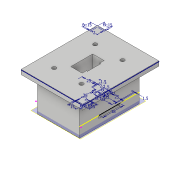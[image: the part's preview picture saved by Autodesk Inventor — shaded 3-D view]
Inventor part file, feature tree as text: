
AUTODESK INVENTOR PART (.ipt)
format: ipt  version: 2017 (Build 210142000, 142)  size: 485,376 bytes
history: native  units: in
note: dims shown in document units (in); Inventor stores cm internally (conversion verified against a paired STEP export)
features: extrude x22, sketch x20, plane x5, fillet x2, other x1, hole x1, chamfer x1
ambient origin geometry x8: Origin, YZ Plane, XZ Plane, XY Plane, X Axis, Y Axis, Z Axis, Center Point
bodies: Solid1 (feature_tree)
feature tree (52):
  plane  "Work Plane1"
  sketch  "Sketch1"  dims[d0=0.9843in d1=0.0067in]
  extrude  "Extrusion1"  Depth=0.0067in
  extrude  "End"  Depth=0.1969in
  extrude  "EndII"  Depth=0.112in
  extrude  "Extrusion4"  Depth=0.112in
  sketch  "Sketch8"  dims[d11=0.1969in d13=0.1969in]
  extrude  "Extrusion8"  Depth=0.1969in
  plane  "Work Plane2"
  sketch  "Sketch12"  dims[d18=2.3278in d19=0.0in d20=0.9843in d21=0.0in]
  other  "Work Point1"
  extrude  "Extrusion10"  Depth=0.9843in TaperAngle=0.0deg
  plane  "Work Plane3"
  extrude  "Extrusion11"  Depth=0.1969in
  plane  "Work Plane4"
  sketch  "Sketch18"  dims[d28=0.0394in d29=0.0394in]
  extrude  "Extrusion15"  Depth=0.0591in TaperAngle=0.0deg
  extrude  "Extrusion16"  Depth=0.0394in
  extrude  "Extrusion17"  [1 undecoded]
  hole  "Hole2"  [1 undecoded]
  sketch  "Sketch19"  dims[d36=0.0039in d37=0.0in d38=-0.1181in]
  extrude  "Extrusion18"  Depth=0.0197in
  extrude  "Extrusion19"  TaperAngle=90.0deg  [1 undecoded]
  extrude  "Extrusion20"  Depth=1.4961in TaperAngle=0.0deg
  extrude  "Extrusion21"  Depth=1.4961in
  extrude  "Extrusion22"  Depth=0.9843in
  extrude  "Extrusion23"  Depth=0.9843in
  fillet  "Fillet1"  Radius=0.9843in
  sketch  "Sketch25"  dims[d51=90.0deg d52=0.0197in]
  extrude  "Extrusion25"  Depth=0.9843in
  sketch  "Sketch28"  dims[d55=1.4961in d56=0.1969in d57=0.0in]
  extrude  "Extrusion27"  Depth=0.3937in
  sketch  "Sketch30"  dims[d60=0.9843in d80=0.9843in]
  extrude  "Extrusion28"  Depth=0.3937in TaperAngle=0.0deg
  extrude  "Extrusion29"  Depth=0.0394in
  chamfer  "Chamfer1"  Distance=0.5906in
  fillet  "Fillet5"  Radius=0.5906in
  extrude  "Extrusion30"  Depth=0.0394in
  plane  "Work Plane6"
  extrude  "Extrusion31"  Depth=0.0394in
  sketch  "Sketch3"  dims[d2=0.1969in d3=0.1969in]
  sketch  "Sketch4"  dims[d4=0.1122in d5=0.112in]
  sketch  "Sketch7"  dims[d7=0.112in d8=0.112in]
  sketch  "Sketch15"  dims[d22=0.9843in d23=0.0in d24=0.1969in]
  sketch  "Sketch17"  dims[d25=0.8661in d26=0.0591in d27=0.0in]
  sketch  "Sketch23"  dims[d49=0.0787in d50=0.0787in]
  sketch  "Sketch26"  dims[d53=0.0in d54=90.0deg]
  sketch  "Sketch29"  dims[d58=0.9843in d59=1.4961in]
  sketch  "Sketch31"  dims[d81=0.9843in d82=0.9843in d83=0.9843in d84=0.9843in d85=0.9843in]
  sketch  "Sketch32"  dims[d86=0.9843in d87=0.9843in d88=0.9843in d89=0.9843in]
  sketch  "Sketch33"  dims[d90=0.9843in d91=0.9843in]
  sketch  "Sketch34"  dims[d96=0.2756in d97=0.75in d98=0.4528in d99=1.5748in d100=0.5635in d101=1.0in d102=0.8108in d103=0.3937in d104=0.3937in d105=0.0in d106=0.5906in d107=0.5906in d108=0.5906in d109=0.5906in d110=0.0787in d111=0.0787in d112=0.0787in d113=0.0787in d120=0.0394in d121=0.0in d122=0.2953in d123=0.0in d124=0.1969in d125=0.0in d126=1.378in d127=0.1181in d128=1.2992in d129=0.6496in d130=0.0in d131=0.1235in d132=0.0in d133=1.1012in d134=0.0in d135=0.0787in d136=0.0787in d137=2.2879in d138=0.0in d139=0.0591in d140=0.0591in d141=0.0591in d142=0.0in d143=0.0394in d144=0.0394in d145=0.0394in d146=0.0394in d147=0.0394in d148=0.0394in d149=0.0394in d150=0.0394in d151=1.1024in d152=0.0in d153=0.0591in d154=0.0591in d155=0.0591in d156=0.0591in d157=0.0591in d158=0.0591in d159=0.0591in d160=0.1181in d161=0.0in d162=0.2362in d163=0.0in d164=0.0567in d168=1.5438in d169=0.0in d171=0.1969in d175=2.3622in d177=0.3937in d178=0.3937in d179=0.5678in d180=1.8937in d181=0.0in d182=0.9188in d183=0.0in d186=0.9188in d187=0.0in d188=1.1024in d189=0.2662in d190=0.0787in d191=45.0deg d192=0.3716in d193=0.0394in d194=0.0354in d195=0.0in d196=-0.1969in d197=0.0in d198=0.0in d199=0.8661in]
note: 3 required parameter values undecoded (feature->parameter linkage not recoverable at this tier; creation-order binding heuristic only, values carry confidence <= 0.55)
